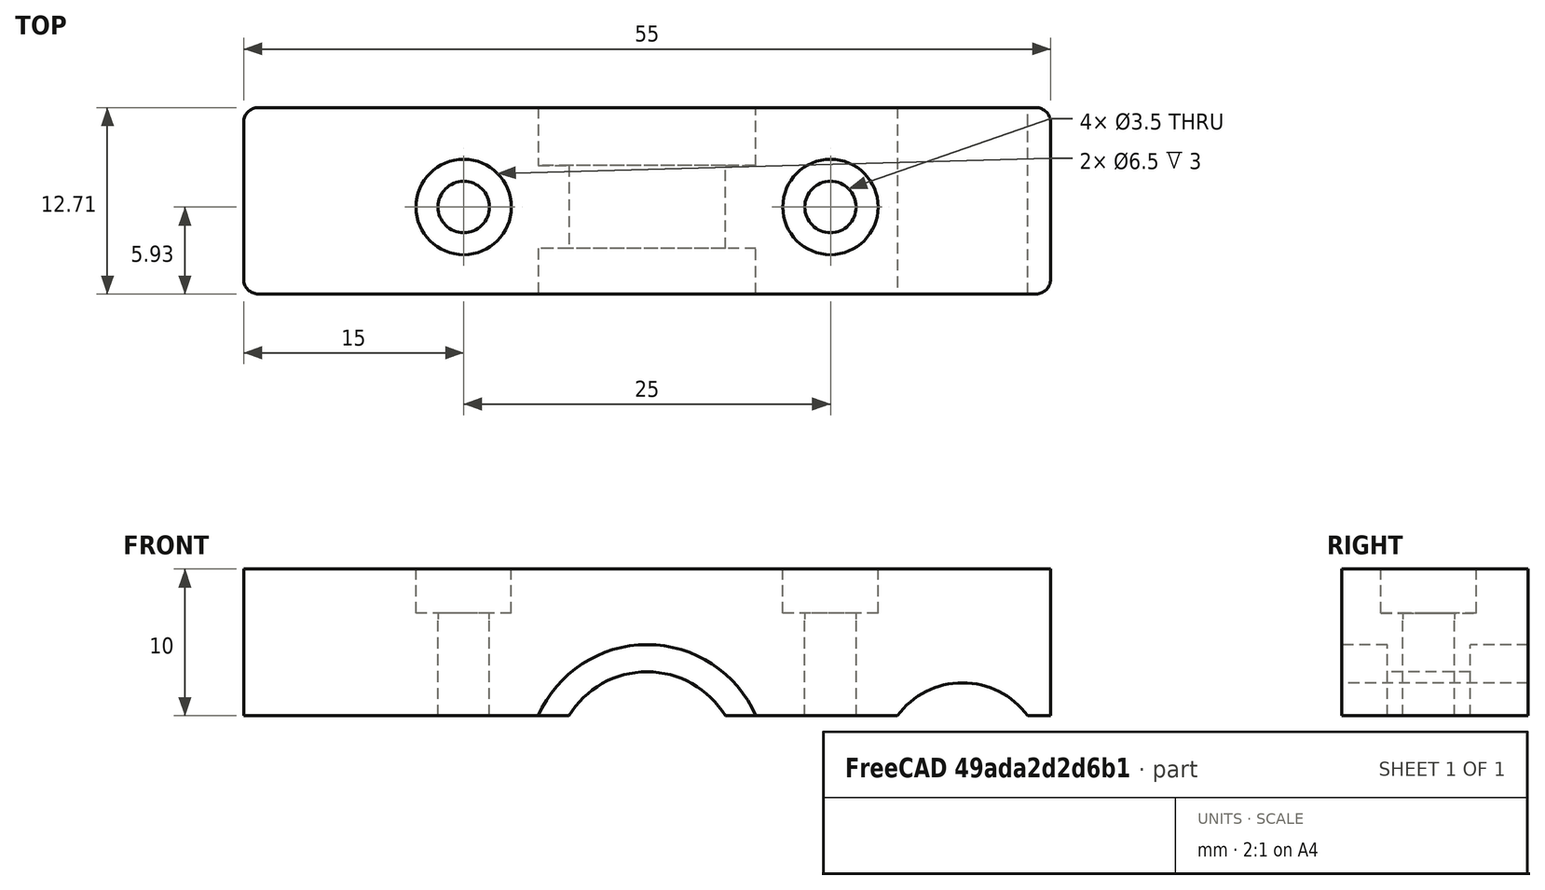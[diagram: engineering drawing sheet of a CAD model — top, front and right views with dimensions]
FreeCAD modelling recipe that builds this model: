
FCSTD DOCUMENT  (FreeCAD 0.17R13519 (Git))
Label: Corelia_0_hotend_retainer
License: All rights reserved
LicenseURL: http://en.wikipedia.org/wiki/All_rights_reserved
objects: PartDesign::Pocket×2, Part::Feature×1, PartDesign::FeatureBase×1, PartDesign::Body×1
note: 7 computed .brp shape members not serialized (recipe doc carries the construction recipe); baked Part::Feature solids carry a one-line shape summary decoded from their .brp

FEATURE [Part::Feature] Part__Feature  label="Retainer"
  shape: bbox 55 x 12.7 x 10 mm, 26 faces (baked)
FEATURE [PartDesign::FeatureBase] BaseFeature
  BaseFeature = -> Part__Feature
FEATURE [PartDesign::Pocket] Pocket
  BaseFeature = -> BaseFeature
  Length = 5
  Length2 = 100
  Profile = -> BaseFeature [Face10]
  Type = 1
FEATURE [PartDesign::Pocket] Pocket001
  BaseFeature = -> Pocket
  Length = 5
  Length2 = 100
  Profile = -> Pocket [Face26]
  Type = 1
FEATURE [PartDesign::Body] Body
  BaseFeature = -> Part__Feature
  Group = -> [BaseFeature,Pocket,Pocket001]
  Origin = -> Origin
  Tip = -> Pocket001
